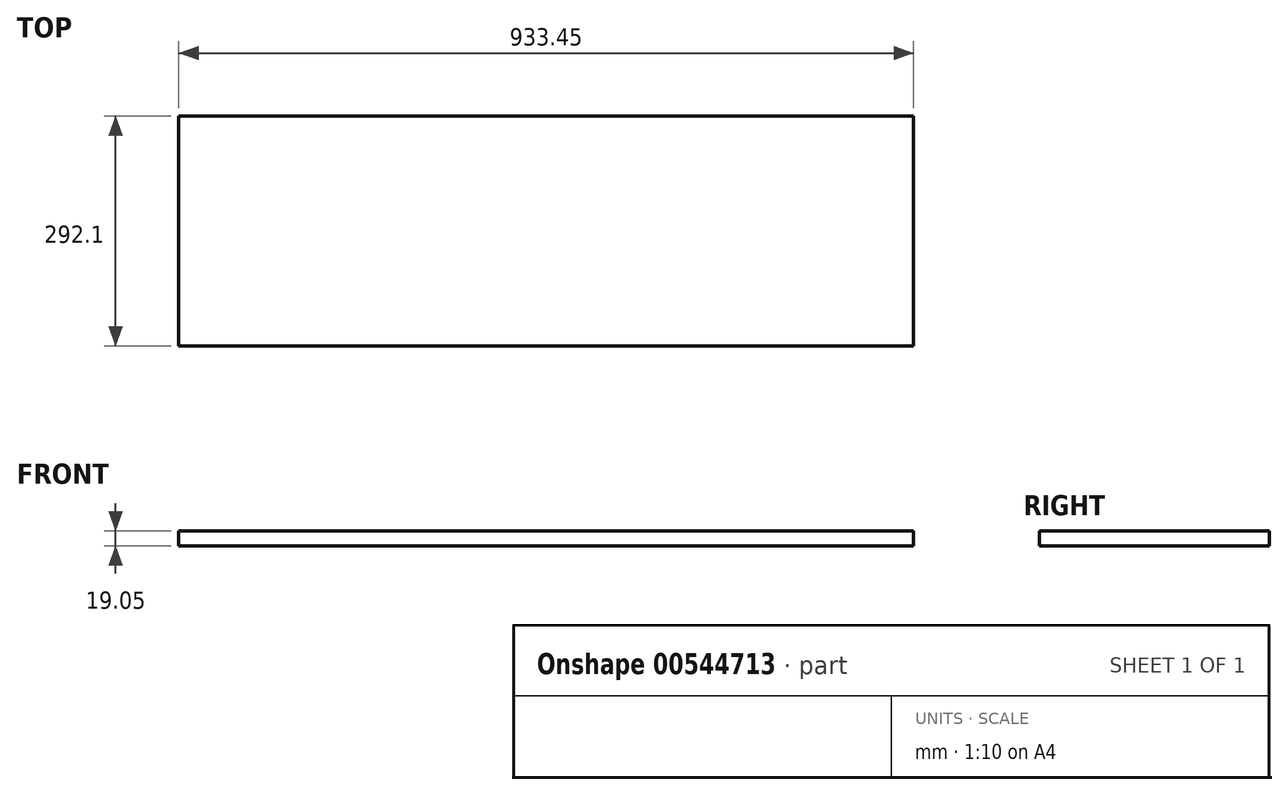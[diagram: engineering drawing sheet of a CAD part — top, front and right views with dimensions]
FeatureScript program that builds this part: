
annotation { "Feature Type Name" : "Feature", "Feature Type Description" : "" }
export const myFeature = defineFeature(function(context is Context, id is Id, definition is map)
    precondition{}
    {
        {
            var Q0;
            Q0=qCreatedBy(makeId("Top.planeOp"),FACE);
            var sketch = newSketch(context, id + "F0", { "sketchPlane" : qUnion([Q0])});
            skLineSegment(sketch, "E0.bottom", {"start": v(0, 0) * mm, "end": v(933.45, 0) * mm});
            skLineSegment(sketch, "E0.top", {"start": v(0, 292.1) * mm, "end": v(933.45, 292.1) * mm});
            skLineSegment(sketch, "E0.left", {"start": v(0, 0) * mm, "end": v(0, 292.1) * mm});
            skLineSegment(sketch, "E0.right", {"start": v(933.45, 0) * mm, "end": v(933.45, 292.1) * mm});
            skSolve(sketch);
        }
        {
            var Q0;
            Q0=makeQuery(id+"F0.imprint","IMPRINT",FACE,{"disambiguationData":[TD([[makeQuery(id+"F0.imprint","IMPRINT",EDGE,{"derivedFrom":sQuery(id+"F0.wireOp",EDGE,"E0.bottom")}),1.0]])]});
            extrude(context, id + "F1", {"entities" : qUnion([Q0]), "depth" : 19.05 * mm, "offsetDistance" : 25.4 * mm});
        }
    });
